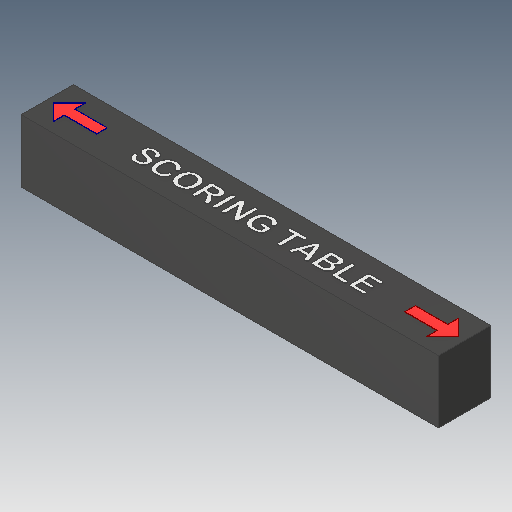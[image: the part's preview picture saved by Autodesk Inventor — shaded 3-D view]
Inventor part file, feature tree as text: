
AUTODESK INVENTOR PART (.ipt)
format: ipt  version: 2023.5 (Build 275446000, 446)  size: 589,824 bytes
history: native  units: in
note: dims shown in document units (in); Inventor stores cm internally (conversion verified against a paired STEP export)
features: other x14, mirror x1
ambient origin geometry x8: Origin, YZ Plane, XZ Plane, XY Plane, X Axis, Y Axis, Z Axis, Center Point
bodies: Solid1 (feature_tree), Solid2 (feature_tree), Solid3 (feature_tree), Solid4 (feature_tree), Solid5 (feature_tree), Solid6 (feature_tree), Solid7 (feature_tree), Solid8 (feature_tree), Solid9 (feature_tree), Solid10 (feature_tree), Solid11 (feature_tree), Solid12 (feature_tree), Solid13 (feature_tree), Solid14 (feature_tree), Solid15 (feature_tree)
feature tree (15):
  other  "Boss-Extrude1"
  other  "Boss-Extrude2[1]"
  other  "Boss-Extrude2[2]"
  other  "Boss-Extrude2[3]"
  other  "Boss-Extrude2[4]"
  other  "Boss-Extrude2[5]"
  other  "Boss-Extrude2[6]"
  other  "Boss-Extrude2[7]"
  other  "Boss-Extrude2[8]"
  other  "Boss-Extrude2[9]"
  other  "Boss-Extrude2[10]"
  other  "Boss-Extrude2[11]"
  other  "Boss-Extrude2[12]"
  other  "Boss-Extrude3"
  mirror  "Mirror1"
